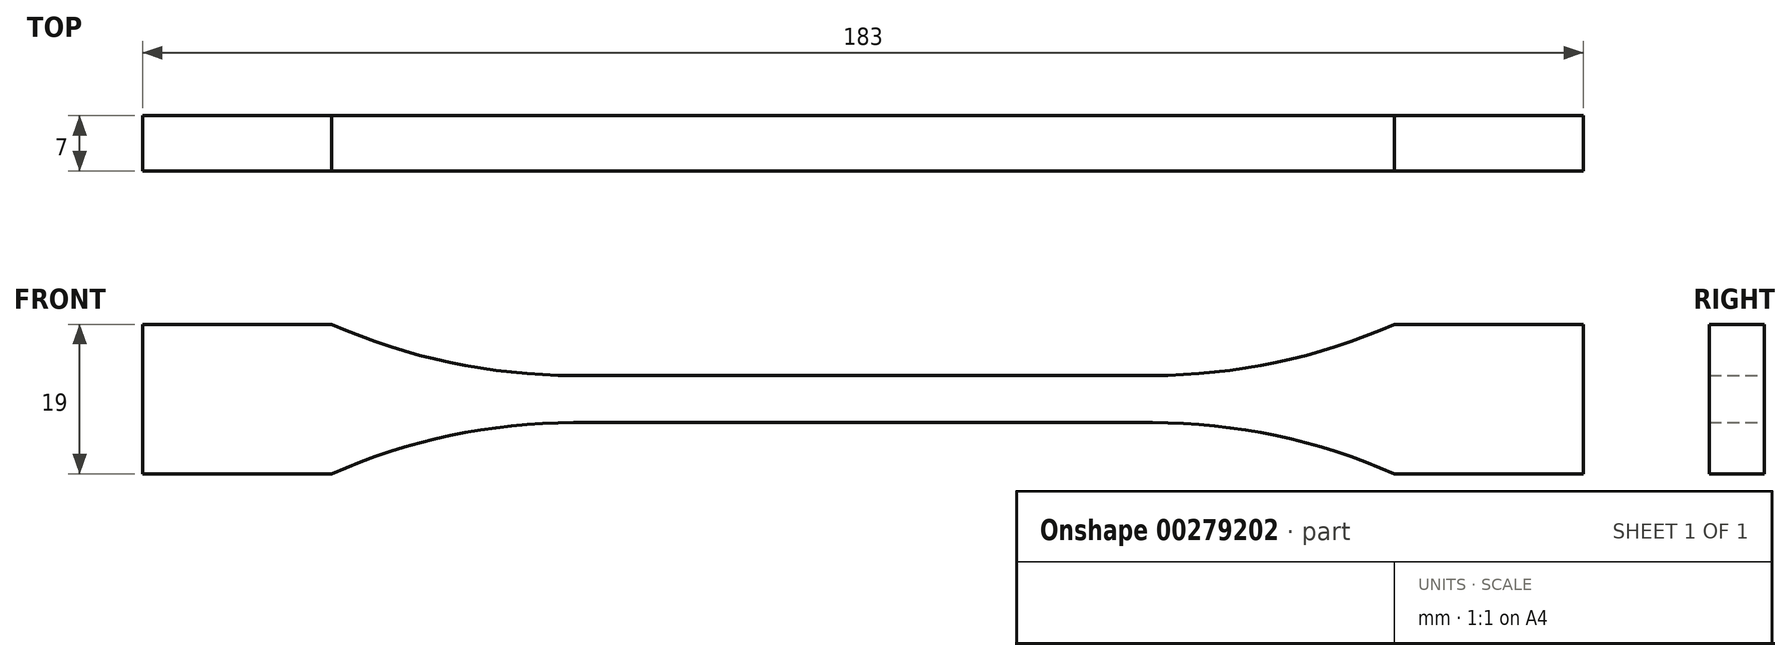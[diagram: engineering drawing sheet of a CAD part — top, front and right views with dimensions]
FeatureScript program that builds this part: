
annotation { "Feature Type Name" : "Feature", "Feature Type Description" : "" }
export const myFeature = defineFeature(function(context is Context, id is Id, definition is map)
    precondition{}
    {
        {
            var Q0;
            Q0=qCreatedBy(makeId("Front.planeOp"),FACE);
            var sketch = newSketch(context, id + "F0", { "sketchPlane" : qUnion([Q0])});
            skLineSegment(sketch, "E0", {"start": v(0, 3) * mm, "end": v(36.75, 3) * mm});
            skArc(sketch, "E1", {"start": v(36.75, 3) * mm, "mid": v(52.46, 4.64) * mm, "end": v(67.5, 9.5) * mm});
            skLineSegment(sketch, "E2", {"start": v(67.5, 9.5) * mm, "end": v(91.5, 9.5) * mm});
            skLineSegment(sketch, "E3.MirrorCS", {"start": v(0, -3) * mm, "end": v(36.75, -3) * mm});
            skLineSegment(sketch, "E4.MirrorCS", {"start": v(67.5, -9.5) * mm, "end": v(91.5, -9.5) * mm});
            skArc(sketch, "E5.MirrorCS", {"start": v(36.75, -3) * mm, "mid": v(52.46, -4.64) * mm, "end": v(67.5, -9.5) * mm});
            skArc(sketch, "E6.MirrorCS", {"start": v(-36.75, -3) * mm, "mid": v(-52.46, -4.64) * mm, "end": v(-67.5, -9.5) * mm});
            skLineSegment(sketch, "E7.MirrorCS", {"start": v(0, 3) * mm, "end": v(-36.75, 3) * mm});
            skArc(sketch, "E8.MirrorCS", {"start": v(-36.75, 3) * mm, "mid": v(-52.46, 4.64) * mm, "end": v(-67.5, 9.5) * mm});
            skLineSegment(sketch, "E9.MirrorCS", {"start": v(-67.5, 9.5) * mm, "end": v(-91.5, 9.5) * mm});
            skLineSegment(sketch, "E10.MirrorCS", {"start": v(0, -3) * mm, "end": v(-36.75, -3) * mm});
            skLineSegment(sketch, "E11.MirrorCS", {"start": v(-67.5, -9.5) * mm, "end": v(-91.5, -9.5) * mm});
            skLineSegment(sketch, "E12", {"start": v(-91.5, -9.5) * mm, "end": v(-91.5, 9.5) * mm});
            skLineSegment(sketch, "E13", {"start": v(91.5, -9.5) * mm, "end": v(91.5, 9.5) * mm});
            skSolve(sketch);
        }
        {
            var Q0;
            Q0 = qSketchRegion(id + "F0", true);
            extrude(context, id + "F1", {"entities" : qUnion([Q0]), "endBound" : BoundingType.SYMMETRIC, "depth" : 7 * mm});
        }
    });
